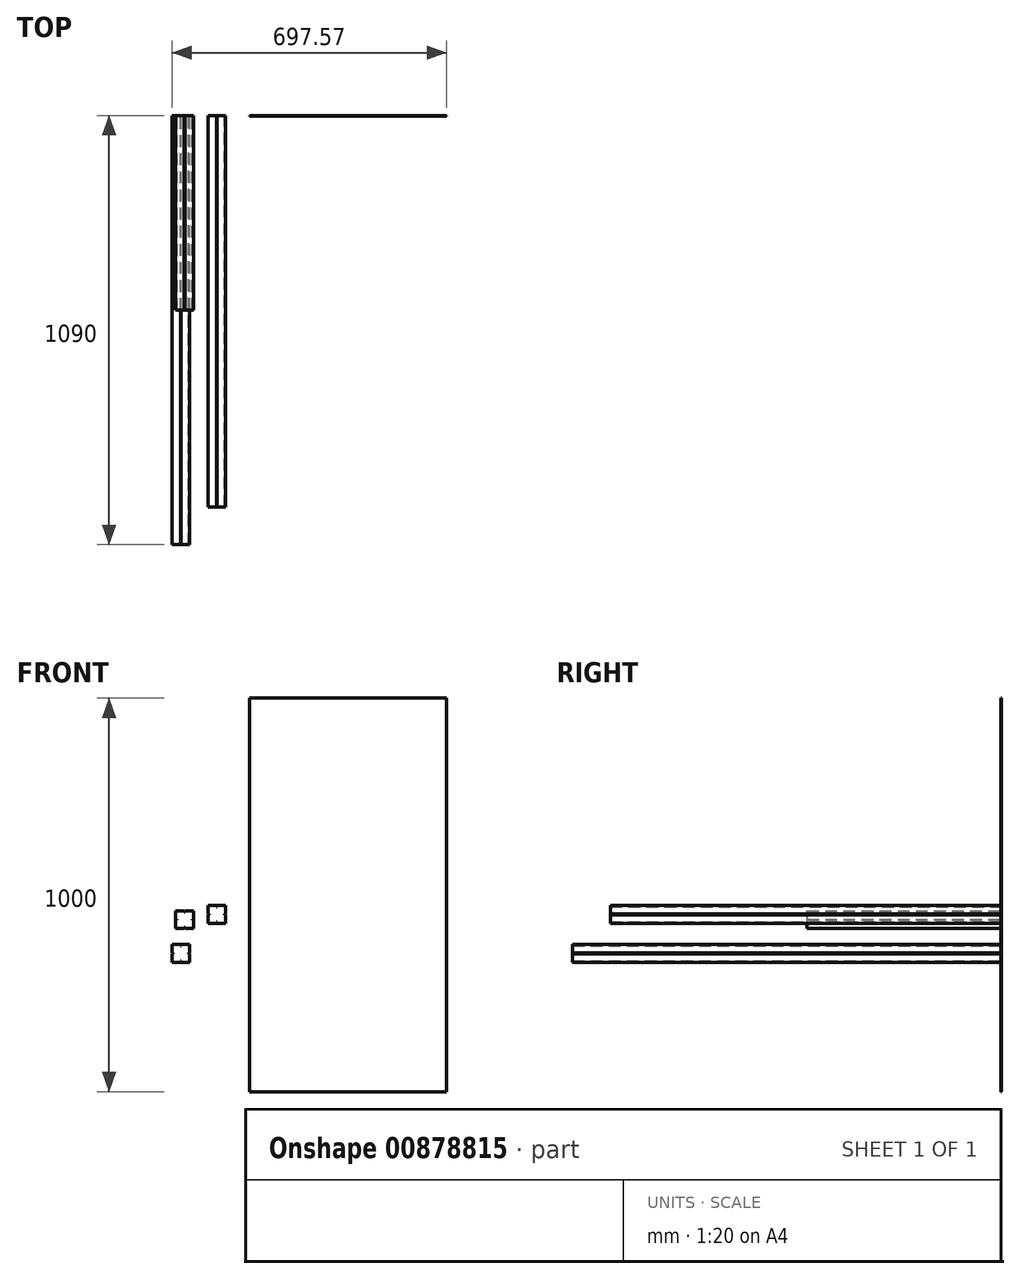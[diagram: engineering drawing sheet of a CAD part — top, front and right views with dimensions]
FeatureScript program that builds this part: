
annotation { "Feature Type Name" : "Feature", "Feature Type Description" : "" }
export const myFeature = defineFeature(function(context is Context, id is Id, definition is map)
    precondition{}
    {
        {
            var Q0;
            Q0=qCreatedBy(makeId("Front.planeOp"),FACE);
            var sketch = newSketch(context, id + "F0", { "sketchPlane" : qUnion([Q0])});
            skLineSegment(sketch, "E0.bottom", {"start": v(-64.7, 53.89) * mm, "end": v(-43.2, 53.89) * mm});
            skLineSegment(sketch, "E0.top", {"start": v(-64.7, 8.89) * mm, "end": v(-43.2, 8.89) * mm});
            skLineSegment(sketch, "E0.left", {"start": v(-64.7, 53.89) * mm, "end": v(-64.7, 32.39) * mm});
            skLineSegment(sketch, "E0.right", {"start": v(-19.7, 53.89) * mm, "end": v(-19.7, 32.39) * mm});
            skLineSegment(sketch, "E1", {"start": v(-42.2, 50.89) * mm, "end": v(-42.2, 11.89) * mm, "construction": true});
            skLineSegment(sketch, "E2", {"start": v(-61.7, 31.39) * mm, "end": v(-22.7, 31.39) * mm, "construction": true});
            skLineSegment(sketch, "E3", {"start": v(-42.2, 11.89) * mm, "end": v(-43.2, 11.89) * mm});
            skLineSegment(sketch, "E4", {"start": v(-43.2, 11.89) * mm, "end": v(-43.2, 8.89) * mm});
            skLineSegment(sketch, "E5.MirrorCS", {"start": v(-41.2, 11.89) * mm, "end": v(-41.2, 8.89) * mm});
            skLineSegment(sketch, "E6.MirrorCS", {"start": v(-42.2, 11.89) * mm, "end": v(-41.2, 11.89) * mm});
            skLineSegment(sketch, "E7.MirrorCS", {"start": v(-43.2, 50.89) * mm, "end": v(-43.2, 53.89) * mm});
            skLineSegment(sketch, "E8.MirrorCS", {"start": v(-42.2, 50.89) * mm, "end": v(-43.2, 50.89) * mm});
            skLineSegment(sketch, "E9.MirrorCS", {"start": v(-41.2, 50.89) * mm, "end": v(-41.2, 53.89) * mm});
            skLineSegment(sketch, "E10.MirrorCS", {"start": v(-42.2, 50.89) * mm, "end": v(-41.2, 50.89) * mm});
            skLineSegment(sketch, "E11", {"start": v(-61.7, 31.39) * mm, "end": v(-61.7, 32.39) * mm});
            skLineSegment(sketch, "E12", {"start": v(-61.7, 32.39) * mm, "end": v(-64.7, 32.39) * mm});
            skLineSegment(sketch, "E13.MirrorCS", {"start": v(-61.7, 30.39) * mm, "end": v(-64.7, 30.39) * mm});
            skLineSegment(sketch, "E14.MirrorCS", {"start": v(-61.7, 31.39) * mm, "end": v(-61.7, 30.39) * mm});
            skLineSegment(sketch, "E15.MirrorCS", {"start": v(-22.7, 32.39) * mm, "end": v(-19.7, 32.39) * mm});
            skLineSegment(sketch, "E16.MirrorCS", {"start": v(-22.7, 30.39) * mm, "end": v(-19.7, 30.39) * mm});
            skLineSegment(sketch, "E17.MirrorCS", {"start": v(-22.7, 31.39) * mm, "end": v(-22.7, 32.39) * mm});
            skLineSegment(sketch, "E18.MirrorCS", {"start": v(-22.7, 31.39) * mm, "end": v(-22.7, 30.39) * mm});
            skLineSegment(sketch, "E19.trimOffspring", {"start": v(-64.7, 30.39) * mm, "end": v(-64.7, 8.89) * mm});
            skPoint(sketch, "E20.orphan", {"position": v(-64.7, 31.39) * mm});
            skLineSegment(sketch, "E21.trimOffspring", {"start": v(-41.2, 53.89) * mm, "end": v(-19.7, 53.89) * mm});
            skPoint(sketch, "E22.orphan", {"position": v(-42.2, 53.89) * mm});
            skLineSegment(sketch, "E23.trimOffspring", {"start": v(-19.7, 30.39) * mm, "end": v(-19.7, 8.89) * mm});
            skPoint(sketch, "E24.orphan", {"position": v(-19.7, 31.39) * mm});
            skLineSegment(sketch, "E25.trimOffspring", {"start": v(-41.2, 8.89) * mm, "end": v(-19.7, 8.89) * mm});
            skPoint(sketch, "E26.orphan", {"position": v(-42.2, 8.89) * mm});
            skSolve(sketch);
        }
        {
            var Q0;
            Q0=makeQuery(id+"F0.imprint","IMPRINT",FACE,{"disambiguationData":[TD([[makeQuery(id+"F0.imprint","IMPRINT",EDGE,{"derivedFrom":sQuery(id+"F0.wireOp",EDGE,"E0.bottom")}),-1.0]])]});
            extrude(context, id + "F1", {"entities" : qUnion([Q0]), "depth" : 494 * mm, "offsetDistance" : 25 * mm});
        }
        {
            var Q0;
            Q0=qCreatedBy(makeId("Front.planeOp"),FACE);
            var sketch = newSketch(context, id + "F2", { "sketchPlane" : qUnion([Q0])});
            skLineSegment(sketch, "E27.bottom", {"start": v(-74.17, -32.2) * mm, "end": v(-52.67, -32.2) * mm});
            skLineSegment(sketch, "E27.top", {"start": v(-74.17, -77.2) * mm, "end": v(-52.67, -77.2) * mm});
            skLineSegment(sketch, "E27.left", {"start": v(-74.17, -32.2) * mm, "end": v(-74.17, -53.7) * mm});
            skLineSegment(sketch, "E27.right", {"start": v(-29.17, -32.2) * mm, "end": v(-29.17, -53.7) * mm});
            skLineSegment(sketch, "E28", {"start": v(-51.67, -35.2) * mm, "end": v(-51.67, -74.2) * mm, "construction": true});
            skLineSegment(sketch, "E29", {"start": v(-71.17, -54.7) * mm, "end": v(-32.17, -54.7) * mm, "construction": true});
            skLineSegment(sketch, "E30", {"start": v(-51.67, -74.2) * mm, "end": v(-52.67, -74.2) * mm});
            skLineSegment(sketch, "E31", {"start": v(-52.67, -74.2) * mm, "end": v(-52.67, -77.2) * mm});
            skLineSegment(sketch, "E32.MirrorCS", {"start": v(-50.67, -74.2) * mm, "end": v(-50.67, -77.2) * mm});
            skLineSegment(sketch, "E33.MirrorCS", {"start": v(-51.67, -74.2) * mm, "end": v(-50.67, -74.2) * mm});
            skLineSegment(sketch, "E34.MirrorCS", {"start": v(-52.67, -35.2) * mm, "end": v(-52.67, -32.2) * mm});
            skLineSegment(sketch, "E35.MirrorCS", {"start": v(-51.67, -35.2) * mm, "end": v(-52.67, -35.2) * mm});
            skLineSegment(sketch, "E36.MirrorCS", {"start": v(-50.67, -35.2) * mm, "end": v(-50.67, -32.2) * mm});
            skLineSegment(sketch, "E37.MirrorCS", {"start": v(-51.67, -35.2) * mm, "end": v(-50.67, -35.2) * mm});
            skLineSegment(sketch, "E38", {"start": v(-71.17, -54.7) * mm, "end": v(-71.17, -53.7) * mm});
            skLineSegment(sketch, "E39", {"start": v(-71.17, -53.7) * mm, "end": v(-74.17, -53.7) * mm});
            skLineSegment(sketch, "E40.MirrorCS", {"start": v(-71.17, -55.7) * mm, "end": v(-74.17, -55.7) * mm});
            skLineSegment(sketch, "E41.MirrorCS", {"start": v(-71.17, -54.7) * mm, "end": v(-71.17, -55.7) * mm});
            skLineSegment(sketch, "E42.MirrorCS", {"start": v(-32.17, -53.7) * mm, "end": v(-29.17, -53.7) * mm});
            skLineSegment(sketch, "E43.MirrorCS", {"start": v(-32.17, -55.7) * mm, "end": v(-29.17, -55.7) * mm});
            skLineSegment(sketch, "E44.MirrorCS", {"start": v(-32.17, -54.7) * mm, "end": v(-32.17, -53.7) * mm});
            skLineSegment(sketch, "E45.MirrorCS", {"start": v(-32.17, -54.7) * mm, "end": v(-32.17, -55.7) * mm});
            skLineSegment(sketch, "E46.trimOffspring", {"start": v(-74.17, -55.7) * mm, "end": v(-74.17, -77.2) * mm});
            skPoint(sketch, "E47.orphan", {"position": v(-74.17, -54.7) * mm});
            skLineSegment(sketch, "E48.trimOffspring", {"start": v(-50.67, -32.2) * mm, "end": v(-29.17, -32.2) * mm});
            skPoint(sketch, "E49.orphan", {"position": v(-51.67, -32.2) * mm});
            skLineSegment(sketch, "E50.trimOffspring", {"start": v(-29.17, -55.7) * mm, "end": v(-29.17, -77.2) * mm});
            skPoint(sketch, "E51.orphan", {"position": v(-29.17, -54.7) * mm});
            skLineSegment(sketch, "E52.trimOffspring", {"start": v(-50.67, -77.2) * mm, "end": v(-29.17, -77.2) * mm});
            skPoint(sketch, "E53.orphan", {"position": v(-51.67, -77.2) * mm});
            skSolve(sketch);
        }
        {
            var Q0;
            Q0 = qSketchRegion(id + "F2", true);
            extrude(context, id + "F3", {"entities" : qUnion([Q0]), "depth" : 1090 * mm, "offsetDistance" : 25 * mm});
        }
        {
            var Q0;
            Q0=qCreatedBy(makeId("Front.planeOp"),FACE);
            var sketch = newSketch(context, id + "F4", { "sketchPlane" : qUnion([Q0])});
            skLineSegment(sketch, "E54.bottom", {"start": v(123.4, 594.12) * mm, "end": v(623.4, 594.12) * mm});
            skLineSegment(sketch, "E54.top", {"start": v(123.4, -405.88) * mm, "end": v(623.4, -405.88) * mm});
            skLineSegment(sketch, "E54.left", {"start": v(123.4, 594.12) * mm, "end": v(123.4, -405.88) * mm});
            skLineSegment(sketch, "E54.right", {"start": v(623.4, 594.12) * mm, "end": v(623.4, -405.88) * mm});
            skSolve(sketch);
        }
        {
            var Q0;
            Q0=makeQuery(id+"F4.imprint","IMPRINT",FACE,{"disambiguationData":[TD([[makeQuery(id+"F4.imprint","IMPRINT",EDGE,{"derivedFrom":sQuery(id+"F4.wireOp",EDGE,"E54.bottom")}),-1.0]])]});
            extrude(context, id + "F5", {"entities" : qUnion([Q0]), "depth" : 2 * mm, "offsetDistance" : 25 * mm});
        }
        {
            var Q0;
            Q0=qCreatedBy(makeId("Front.planeOp"),FACE);
            var sketch = newSketch(context, id + "F6", { "sketchPlane" : qUnion([Q0])});
            skLineSegment(sketch, "E55.bottom", {"start": v(17.3, 66.84) * mm, "end": v(38.8, 66.84) * mm});
            skLineSegment(sketch, "E55.top", {"start": v(17.3, 21.84) * mm, "end": v(38.8, 21.84) * mm});
            skLineSegment(sketch, "E55.left", {"start": v(17.3, 66.84) * mm, "end": v(17.3, 45.34) * mm});
            skLineSegment(sketch, "E55.right", {"start": v(62.3, 66.84) * mm, "end": v(62.3, 45.34) * mm});
            skLineSegment(sketch, "E56", {"start": v(39.8, 63.84) * mm, "end": v(39.8, 24.84) * mm, "construction": true});
            skLineSegment(sketch, "E57", {"start": v(20.3, 44.34) * mm, "end": v(59.3, 44.34) * mm, "construction": true});
            skLineSegment(sketch, "E58", {"start": v(39.8, 24.84) * mm, "end": v(38.8, 24.84) * mm});
            skLineSegment(sketch, "E59", {"start": v(38.8, 24.84) * mm, "end": v(38.8, 21.84) * mm});
            skLineSegment(sketch, "E60.MirrorCS", {"start": v(40.8, 24.84) * mm, "end": v(40.8, 21.84) * mm});
            skLineSegment(sketch, "E61.MirrorCS", {"start": v(39.8, 24.84) * mm, "end": v(40.8, 24.84) * mm});
            skLineSegment(sketch, "E62.MirrorCS", {"start": v(38.8, 63.84) * mm, "end": v(38.8, 66.84) * mm});
            skLineSegment(sketch, "E63.MirrorCS", {"start": v(39.8, 63.84) * mm, "end": v(38.8, 63.84) * mm});
            skLineSegment(sketch, "E64.MirrorCS", {"start": v(40.8, 63.84) * mm, "end": v(40.8, 66.84) * mm});
            skLineSegment(sketch, "E65.MirrorCS", {"start": v(39.8, 63.84) * mm, "end": v(40.8, 63.84) * mm});
            skLineSegment(sketch, "E66", {"start": v(20.3, 44.34) * mm, "end": v(20.3, 45.34) * mm});
            skLineSegment(sketch, "E67", {"start": v(20.3, 45.34) * mm, "end": v(17.3, 45.34) * mm});
            skLineSegment(sketch, "E68.MirrorCS", {"start": v(20.3, 43.34) * mm, "end": v(17.3, 43.34) * mm});
            skLineSegment(sketch, "E69.MirrorCS", {"start": v(20.3, 44.34) * mm, "end": v(20.3, 43.34) * mm});
            skLineSegment(sketch, "E70.MirrorCS", {"start": v(59.3, 45.34) * mm, "end": v(62.3, 45.34) * mm});
            skLineSegment(sketch, "E71.MirrorCS", {"start": v(59.3, 43.34) * mm, "end": v(62.3, 43.34) * mm});
            skLineSegment(sketch, "E72.MirrorCS", {"start": v(59.3, 44.34) * mm, "end": v(59.3, 45.34) * mm});
            skLineSegment(sketch, "E73.MirrorCS", {"start": v(59.3, 44.34) * mm, "end": v(59.3, 43.34) * mm});
            skLineSegment(sketch, "E74.trimOffspring", {"start": v(17.3, 43.34) * mm, "end": v(17.3, 21.84) * mm});
            skPoint(sketch, "E75.orphan", {"position": v(17.3, 44.34) * mm});
            skLineSegment(sketch, "E76.trimOffspring", {"start": v(40.8, 66.84) * mm, "end": v(62.3, 66.84) * mm});
            skPoint(sketch, "E77.orphan", {"position": v(39.8, 66.84) * mm});
            skLineSegment(sketch, "E78.trimOffspring", {"start": v(62.3, 43.34) * mm, "end": v(62.3, 21.84) * mm});
            skPoint(sketch, "E79.orphan", {"position": v(62.3, 44.34) * mm});
            skLineSegment(sketch, "E80.trimOffspring", {"start": v(40.8, 21.84) * mm, "end": v(62.3, 21.84) * mm});
            skPoint(sketch, "E81.orphan", {"position": v(39.8, 21.84) * mm});
            skSolve(sketch);
        }
        {
            var Q0;
            Q0 = qSketchRegion(id + "F6", true);
            extrude(context, id + "F7", {"entities" : qUnion([Q0]), "depth" : 994 * mm, "offsetDistance" : 25 * mm});
        }
    });
